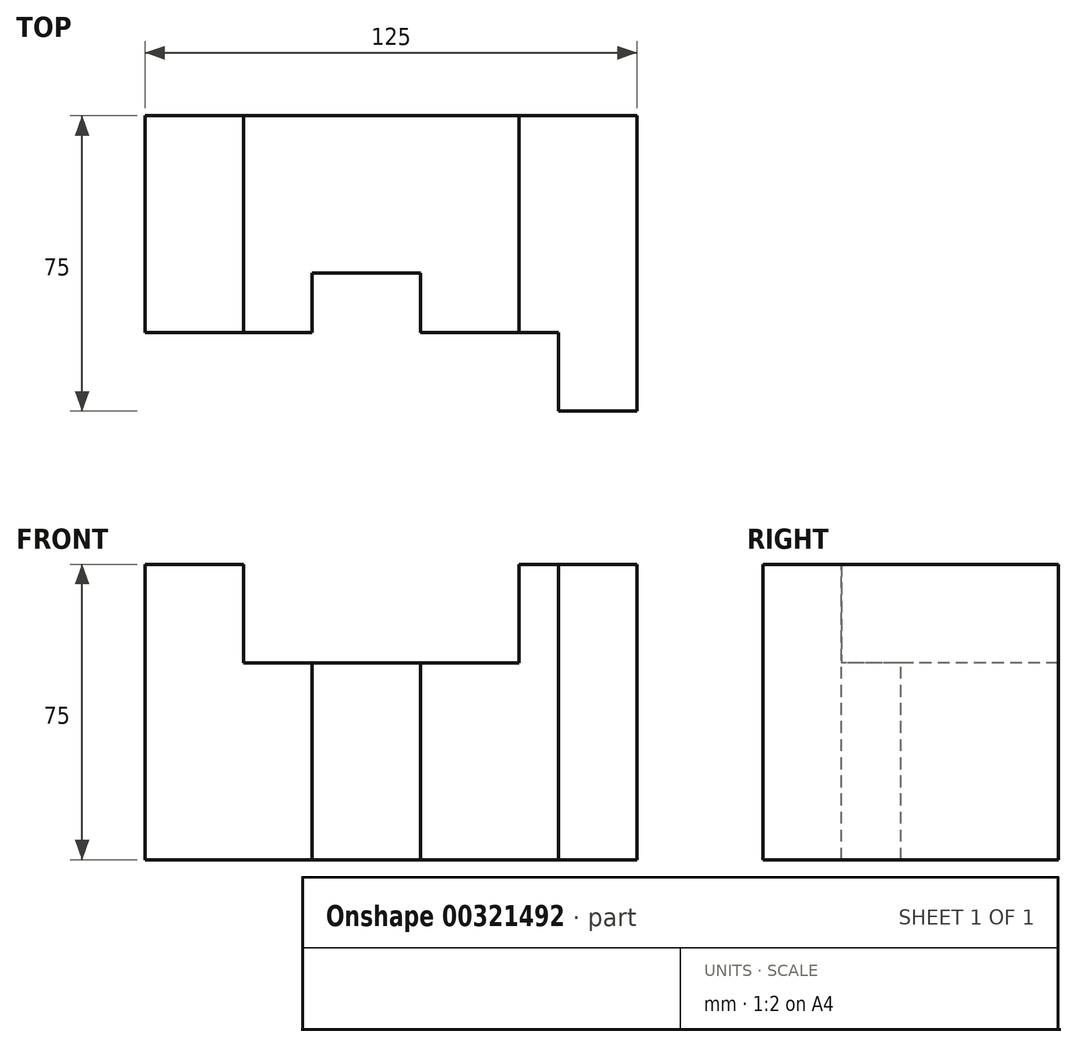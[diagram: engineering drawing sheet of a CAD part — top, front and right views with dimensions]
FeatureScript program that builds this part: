
annotation { "Feature Type Name" : "Feature", "Feature Type Description" : "" }
export const myFeature = defineFeature(function(context is Context, id is Id, definition is map)
    precondition{}
    {
        {
            var Q0;
            Q0=qCreatedBy(makeId("Top.planeOp"),FACE);
            var sketch = newSketch(context, id + "F0", { "sketchPlane" : qUnion([Q0])});
            skLineSegment(sketch, "E0", {"start": v(0, 0) * mm, "end": v(0, 55) * mm});
            skLineSegment(sketch, "E1", {"start": v(0, 55) * mm, "end": v(125, 55) * mm});
            skLineSegment(sketch, "E2", {"start": v(125, 55) * mm, "end": v(125, -20) * mm});
            skLineSegment(sketch, "E3", {"start": v(125, -20) * mm, "end": v(105, -20) * mm});
            skLineSegment(sketch, "E4", {"start": v(105, -20) * mm, "end": v(105, 0) * mm});
            skLineSegment(sketch, "E5", {"start": v(105, 0) * mm, "end": v(70, 0) * mm});
            skLineSegment(sketch, "E6", {"start": v(70, 0) * mm, "end": v(70, 15) * mm});
            skLineSegment(sketch, "E7", {"start": v(70, 15) * mm, "end": v(42.5, 15) * mm});
            skLineSegment(sketch, "E8", {"start": v(42.5, 15) * mm, "end": v(42.5, 0) * mm});
            skLineSegment(sketch, "E9", {"start": v(42.5, 0) * mm, "end": v(0, 0) * mm});
            skSolve(sketch);
        }
        {
            var Q0;
            Q0 = qSketchRegion(id + "F0", true);
            extrude(context, id + "F1", {"entities" : qUnion([Q0]), "oppositeDirection" : true, "depth" : 75 * mm});
        }
        {
            var Q0;
            Q0=qCreatedBy(makeId("Front.planeOp"),FACE);
            var sketch = newSketch(context, id + "F2", { "sketchPlane" : qUnion([Q0])});
            skLineSegment(sketch, "E10.bottom", {"start": v(25, 0) * mm, "end": v(95, 0) * mm});
            skLineSegment(sketch, "E10.top", {"start": v(25, -25) * mm, "end": v(95, -25) * mm});
            skLineSegment(sketch, "E10.left", {"start": v(25, 0) * mm, "end": v(25, -25) * mm});
            skLineSegment(sketch, "E10.right", {"start": v(95, 0) * mm, "end": v(95, -25) * mm});
            skSolve(sketch);
        }
        {
            var Q0;
            Q0 = qSketchRegion(id + "F2", true);
            extrude(context, id + "F3", {"entities" : qUnion([Q0]), "operationType" : NewBodyOperationType.REMOVE, "endBound" : BoundingType.THROUGH_ALL, "oppositeDirection" : true, "depth" : 25 * mm});
        }
    });
